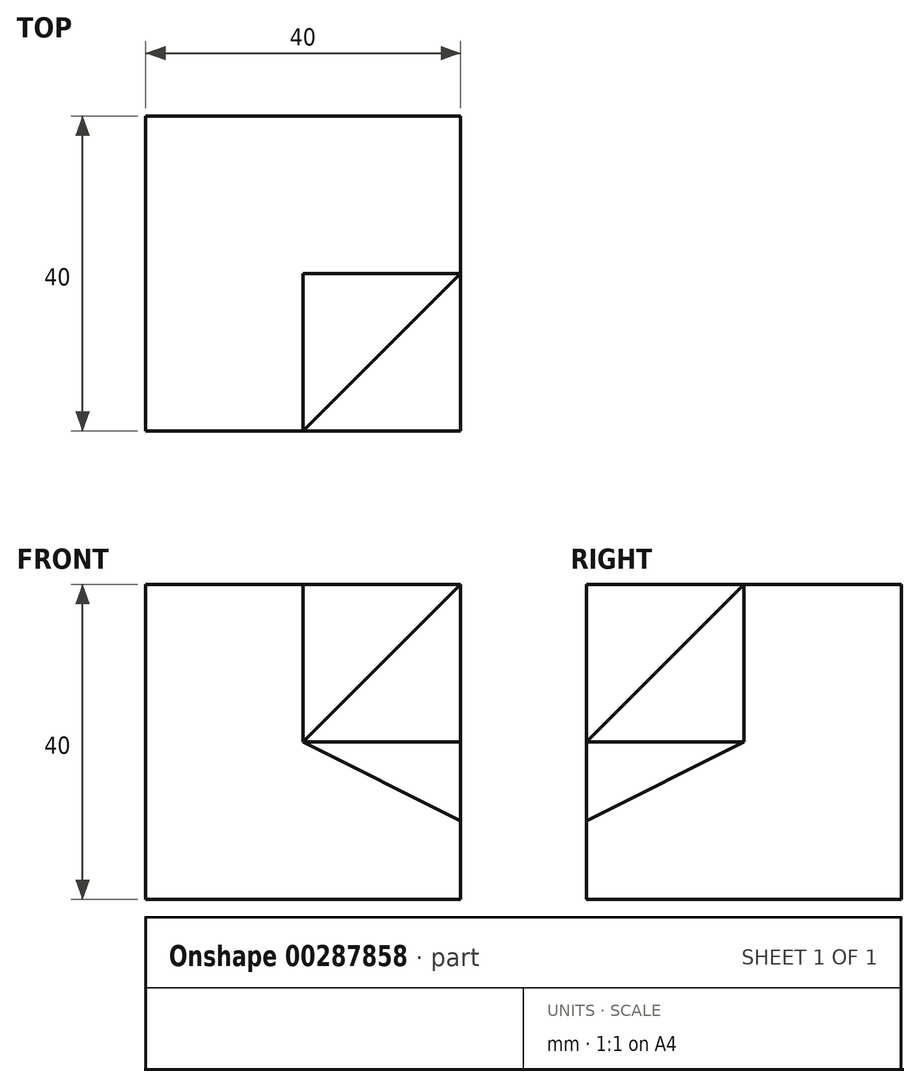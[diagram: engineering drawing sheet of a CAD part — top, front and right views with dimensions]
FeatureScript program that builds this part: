
annotation { "Feature Type Name" : "Feature", "Feature Type Description" : "" }
export const myFeature = defineFeature(function(context is Context, id is Id, definition is map)
    precondition{}
    {
        {
            var Q0;
            Q0=qCreatedBy(makeId("Front.planeOp"),FACE);
            var sketch = newSketch(context, id + "F0", { "sketchPlane" : qUnion([Q0])});
            skLineSegment(sketch, "E0.bottom", {"start": v(0, 0) * mm, "end": v(40, 0) * mm});
            skLineSegment(sketch, "E0.top", {"start": v(0, 40) * mm, "end": v(40, 40) * mm});
            skLineSegment(sketch, "E0.left", {"start": v(0, 0) * mm, "end": v(0, 40) * mm});
            skLineSegment(sketch, "E0.right", {"start": v(40, 0) * mm, "end": v(40, 40) * mm});
            skSolve(sketch);
        }
        {
            var Q0;
            Q0=qSketchRegion(id+"F0",true);
            extrude(context, id + "F1", {"entities" : qUnion([Q0]), "depth" : 40 * mm});
        }
        {
            var Q0;
            Q0=makeQuery(id+"F1.opExtrude","CAP_FACE",FACE,{"disambiguationData":[OSD([sQuery(id+"F0.wireOp",EDGE,"E0.bottom"),sQuery(id+"F0.wireOp",EDGE,"E0.top"),sQuery(id+"F0.wireOp",EDGE,"E0.left"),sQuery(id+"F0.wireOp",EDGE,"E0.right")])],"isStart":false});
            var sketch = newSketch(context, id + "F2", { "sketchPlane" : qUnion([Q0])});
            skPoint(sketch, "E1.oppositeSnap0", {"position": v(20, 0) * mm});
            skPoint(sketch, "E1.oppositeSnap1", {"position": v(0, 20) * mm});
            skLineSegment(sketch, "E1.bottom", {"start": v(40, 40) * mm, "end": v(20, 40) * mm});
            skLineSegment(sketch, "E1.top", {"start": v(40, 20) * mm, "end": v(20, 20) * mm});
            skLineSegment(sketch, "E1.left", {"start": v(40, 40) * mm, "end": v(40, 20) * mm});
            skLineSegment(sketch, "E1.right", {"start": v(20, 40) * mm, "end": v(20, 20) * mm});
            skSolve(sketch);
        }
        {
            var Q0;
            Q0=qSketchRegion(id+"F2",true);
            extrude(context, id + "F3", {"entities" : qUnion([Q0]), "operationType" : NewBodyOperationType.REMOVE, "oppositeDirection" : true, "depth" : 20 * mm});
        }
        {
            var Q0;
            Q0=makeQuery(id+"F1.opExtrude","CAP_EDGE",EDGE,{"disambiguationData":[OSD([sQuery(id+"F0.wireOp",EDGE,"E0.right")])],"isStart":false});
            cPoint(context, id + "F4", {"entities" : qUnion([Q0]), "parameter" : 0.5});
        }
        {
            var Q0;
            Q0=makeQuery(id+"F3.boolean.opBoolean","COPY",VERTEX,{"derivedFrom":makeQuery(id+"F3.opExtrude","CAP_VERTEX",VERTEX,{"disambiguationData":[OSD([sQuery(id+"F0.wireOp",EDGE,"E0.right"),sQuery(id+"F2.wireOp",EDGE,"E1.top"),sQuery(id+"F2.wireOp",EDGE,"E1.left")])],"isStart":false})});
            var Q1;
            Q1=makeQuery(id+"F3.boolean.opBoolean","COPY",VERTEX,{"derivedFrom":makeQuery(id+"F3.opExtrude","CAP_VERTEX",VERTEX,{"disambiguationData":[OSD([sQuery(id+"F2.wireOp",EDGE,"E1.top"),sQuery(id+"F2.wireOp",EDGE,"E1.right")])],"isStart":true})});
            var Q2;
            Q2=qCreatedBy(id+"F4",VERTEX);
            cPlane(context, id + "F5", {"entities" : qUnion([Q0, Q1, Q2]), "cplaneType" : CPlaneType.THREE_POINT, "offset" : 25 * mm, "width" : 150 * mm, "height" : 150 * mm});
        }
        {
            var Q0;
            Q0=qCreatedBy(id+"F5.planeOp",FACE);
            var sketch = newSketch(context, id + "F6", { "sketchPlane" : qUnion([Q0])});
            skPoint(sketch, "E2.0", {"position": v(25.56, 8.94) * mm});
            skPoint(sketch, "E3.0", {"position": v(3.65, 26.83) * mm});
            skPoint(sketch, "E4.0", {"position": v(25.56, 31.3) * mm});
            skLineSegment(sketch, "E5", {"start": v(25.56, 8.94) * mm, "end": v(3.65, 26.83) * mm});
            skLineSegment(sketch, "E6", {"start": v(25.56, 31.3) * mm, "end": v(3.65, 26.83) * mm});
            skLineSegment(sketch, "E7", {"start": v(25.56, 8.94) * mm, "end": v(25.56, 31.3) * mm});
            skSolve(sketch);
        }
        {
            var Q0;
            Q0=qSketchRegion(id+"F6",true);
            extrude(context, id + "F7", {"entities" : qUnion([Q0]), "operationType" : NewBodyOperationType.REMOVE, "endBound" : BoundingType.THROUGH_ALL, "oppositeDirection" : true, "depth" : 25 * mm});
        }
        {
            var Q0;
            Q0=makeQuery(id+"F3.boolean.opBoolean","COPY",FACE,{"derivedFrom":makeQuery(id+"F3.opExtrude","SWEPT_FACE",FACE,{"disambiguationData":[OSD([sQuery(id+"F2.wireOp",EDGE,"E1.right")])]})});
            var sketch = newSketch(context, id + "F8", { "sketchPlane" : qUnion([Q0])});
            skLineSegment(sketch, "E8", {"start": v(-20, 40) * mm, "end": v(-40, 20) * mm});
            skLineSegment(sketch, "E9.0", {"start": v(-20, 40) * mm, "end": v(-20, 20) * mm});
            skLineSegment(sketch, "E10.0", {"start": v(-20, 20) * mm, "end": v(-40, 20) * mm});
            skSolve(sketch);
        }
        {
            var Q0;
            Q0 = qSketchRegion(id + "F8", true);
            var Q1;
            Q1=makeQuery(id+"F1.opExtrude","SWEPT_FACE",FACE,{"disambiguationData":[OSD([sQuery(id+"F0.wireOp",EDGE,"E0.right")])]});
            extrude(context, id + "F9", {"entities" : qUnion([Q0]), "operationType" : NewBodyOperationType.ADD, "endBound" : BoundingType.UP_TO_SURFACE, "endBoundEntityFace" : qUnion([Q1]), "depth" : 25 * mm});
        }
        {
            var Q0;
            Q0=makeQuery(id+"F9.opExtrude","SWEPT_FACE",FACE,{"disambiguationData":[OSD([sQuery(id+"F8.wireOp",EDGE,"E10.0")])]});
            var sketch = newSketch(context, id + "F10", { "sketchPlane" : qUnion([Q0])});
            skLineSegment(sketch, "E11.0", {"start": v(40, 20) * mm, "end": v(20, 40) * mm});
            skLineSegment(sketch, "E12.0", {"start": v(40, 40) * mm, "end": v(20, 40) * mm});
            skLineSegment(sketch, "E13.0", {"start": v(40, 20) * mm, "end": v(40, 40) * mm});
            skSolve(sketch);
        }
        {
            var Q0;
            Q0 = qSketchRegion(id + "F10", true);
            var Q1;
            Q1=makeQuery(id+"F1.opExtrude","SWEPT_FACE",FACE,{"disambiguationData":[OSD([sQuery(id+"F0.wireOp",EDGE,"E0.top")])]});
            extrude(context, id + "F11", {"entities" : qUnion([Q0]), "operationType" : NewBodyOperationType.REMOVE, "endBound" : BoundingType.UP_TO_SURFACE, "oppositeDirection" : true, "endBoundEntityFace" : qUnion([Q1]), "depth" : 25 * mm});
        }
    });
